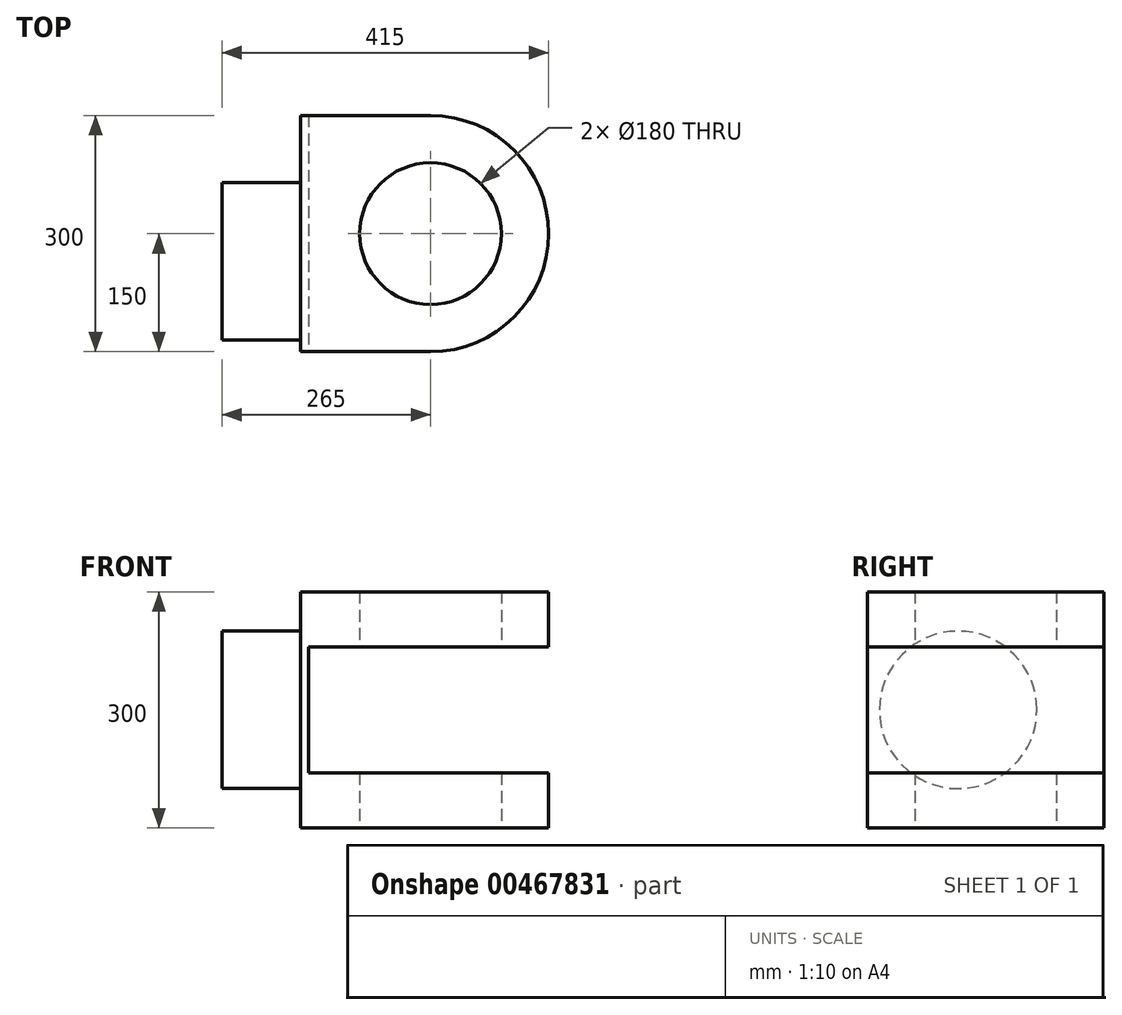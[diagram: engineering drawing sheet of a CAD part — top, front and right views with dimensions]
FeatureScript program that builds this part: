
annotation { "Feature Type Name" : "Feature", "Feature Type Description" : "" }
export const myFeature = defineFeature(function(context is Context, id is Id, definition is map)
    precondition{}
    {
        {
            var Q0;
            Q0=qCreatedBy(makeId("Top.planeOp"),FACE);
            var sketch = newSketch(context, id + "F0", { "sketchPlane" : qUnion([Q0])});
            skLineSegment(sketch, "E0.bottom", {"start": v(82.5, -150) * mm, "end": v(-82.5, -150) * mm});
            skLineSegment(sketch, "E0.top", {"start": v(82.5, 150) * mm, "end": v(-82.5, 150) * mm});
            skPoint(sketch, "E0.middle", {"position": v(0, 0) * mm});
            skArc(sketch, "E1", {"start": v(-82.5, 150) * mm, "mid": v(-232.5, 0) * mm, "end": v(-82.5, -150) * mm});
            skArc(sketch, "E2", {"start": v(82.5, -150) * mm, "mid": v(232.5, 0) * mm, "end": v(82.5, 150) * mm});
            skSolve(sketch);
        }
        {
            var Q0;
            Q0 = qSketchRegion(id + "F0", true);
            extrude(context, id + "F1", {"entities" : qUnion([Q0]), "depth" : 300 * mm});
        }
        {
            var Q0;
            Q0=makeQuery(id+"F1.opExtrude","CAP_FACE",FACE,{"disambiguationData":[OSD([sQuery(id+"F0.wireOp",EDGE,"E0.bottom"),sQuery(id+"F0.wireOp",EDGE,"E0.top"),sQuery(id+"F0.wireOp",EDGE,"E1"),sQuery(id+"F0.wireOp",EDGE,"E2")])],"isStart":true});
            var sketch = newSketch(context, id + "F2", { "sketchPlane" : qUnion([Q0])});
            skCircle(sketch, "E3", {"center": v(82.5, 0) * mm, "radius": 90 * mm});
            skPoint(sketch, "E4.center.orphan", {"position": v(-82.5, 0) * mm});
            skLineSegment(sketch, "E5", {"start": v(-82.5, -150) * mm, "end": v(-82.5, 150) * mm});
            skLineSegment(sketch, "E6", {"start": v(-82.5, 150) * mm, "end": v(-450.4, 150) * mm});
            skLineSegment(sketch, "E7", {"start": v(-450.4, 150) * mm, "end": v(-450.4, -150) * mm});
            skLineSegment(sketch, "E8", {"start": v(-450.4, -150) * mm, "end": v(-82.5, -150) * mm});
            skSolve(sketch);
        }
        {
            var Q0;
            Q0 = qSketchRegion(id + "F2", true);
            extrude(context, id + "F3", {"entities" : qUnion([Q0]), "operationType" : NewBodyOperationType.REMOVE, "oppositeDirection" : true, "depth" : 501 * mm});
        }
        {
            var Q0;
            Q0=makeQuery(id+"F1.opExtrude","SWEPT_FACE",FACE,{"disambiguationData":[OSD([sQuery(id+"F0.wireOp",EDGE,"E0.bottom")])]});
            var sketch = newSketch(context, id + "F4", { "sketchPlane" : qUnion([Q0])});
            skLineSegment(sketch, "E9.bottom", {"start": v(-72.5, 70) * mm, "end": v(237.5, 70) * mm});
            skLineSegment(sketch, "E9.top", {"start": v(-72.5, 230) * mm, "end": v(237.5, 230) * mm});
            skLineSegment(sketch, "E9.left", {"start": v(-72.5, 70) * mm, "end": v(-72.5, 230) * mm});
            skLineSegment(sketch, "E9.right", {"start": v(237.5, 70) * mm, "end": v(237.5, 230) * mm});
            skPoint(sketch, "E9.middle", {"position": v(82.5, 150) * mm});
            skSolve(sketch);
        }
        {
            var Q0;
            {var subQ0=sQuery(id+"F4.wireOp",EDGE,"E9.right");Q0=makeQuery(id+"F4.imprint","IMPRINT",FACE,{"disambiguationData":[TD([[makeQuery(id+"F4.imprint","IMPRINT",EDGE,{"derivedFrom":subQ0}),1.0]])]});}
            var Q1;
            {var subQ0=sQuery(id+"F4.wireOp",EDGE,"E9.left");Q1=makeQuery(id+"F4.imprint","IMPRINT",FACE,{"disambiguationData":[TD([[makeQuery(id+"F4.imprint","IMPRINT",EDGE,{"derivedFrom":subQ0}),-1.0]])]});}
            extrude(context, id + "F5", {"entities" : qUnion([Q0, Q1]), "operationType" : NewBodyOperationType.REMOVE, "oppositeDirection" : true, "depth" : 501 * mm});
        }
        {
            var Q0;
            Q0=makeQuery(id+"F3.boolean.opBoolean","COPY",FACE,{"derivedFrom":makeQuery(id+"F3.opExtrude","SWEPT_FACE",FACE,{"disambiguationData":[OSD([sQuery(id+"F2.wireOp",EDGE,"E5")])]})});
            var sketch = newSketch(context, id + "F6", { "sketchPlane" : qUnion([Q0])});
            skCircle(sketch, "E10", {"center": v(35, 150) * mm, "radius": 100 * mm});
            skPoint(sketch, "E10.centerSnap0", {"position": v(150, 150) * mm});
            skPoint(sketch, "E10.centerSnap1", {"position": v(0, 300) * mm});
            skSolve(sketch);
        }
        {
            var Q0;
            Q0 = qSketchRegion(id + "F6", true);
            extrude(context, id + "F7", {"entities" : qUnion([Q0]), "operationType" : NewBodyOperationType.ADD, "depth" : 100 * mm});
        }
    });
